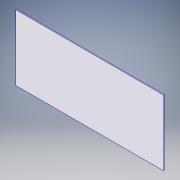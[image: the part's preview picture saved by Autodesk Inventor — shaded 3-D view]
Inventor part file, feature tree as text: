
AUTODESK INVENTOR PART (.ipt)
format: ipt  version: 2019 (Build 230136000, 136)  size: 91,136 bytes
history: native  units: mm
features: extrude x1, sketch x1
ambient origin geometry x8: Origin, YZ Plane, XZ Plane, XY Plane, X Axis, Y Axis, Z Axis, Center Point
bodies: Solid1 (feature_tree)
feature tree (2):
  extrude  "Extrusion1"  Depth=800.0mm
  sketch  "Sketch1"  dims[d0=1800.0mm d1=800.0mm d2=10.0mm d3=0.0mm]
